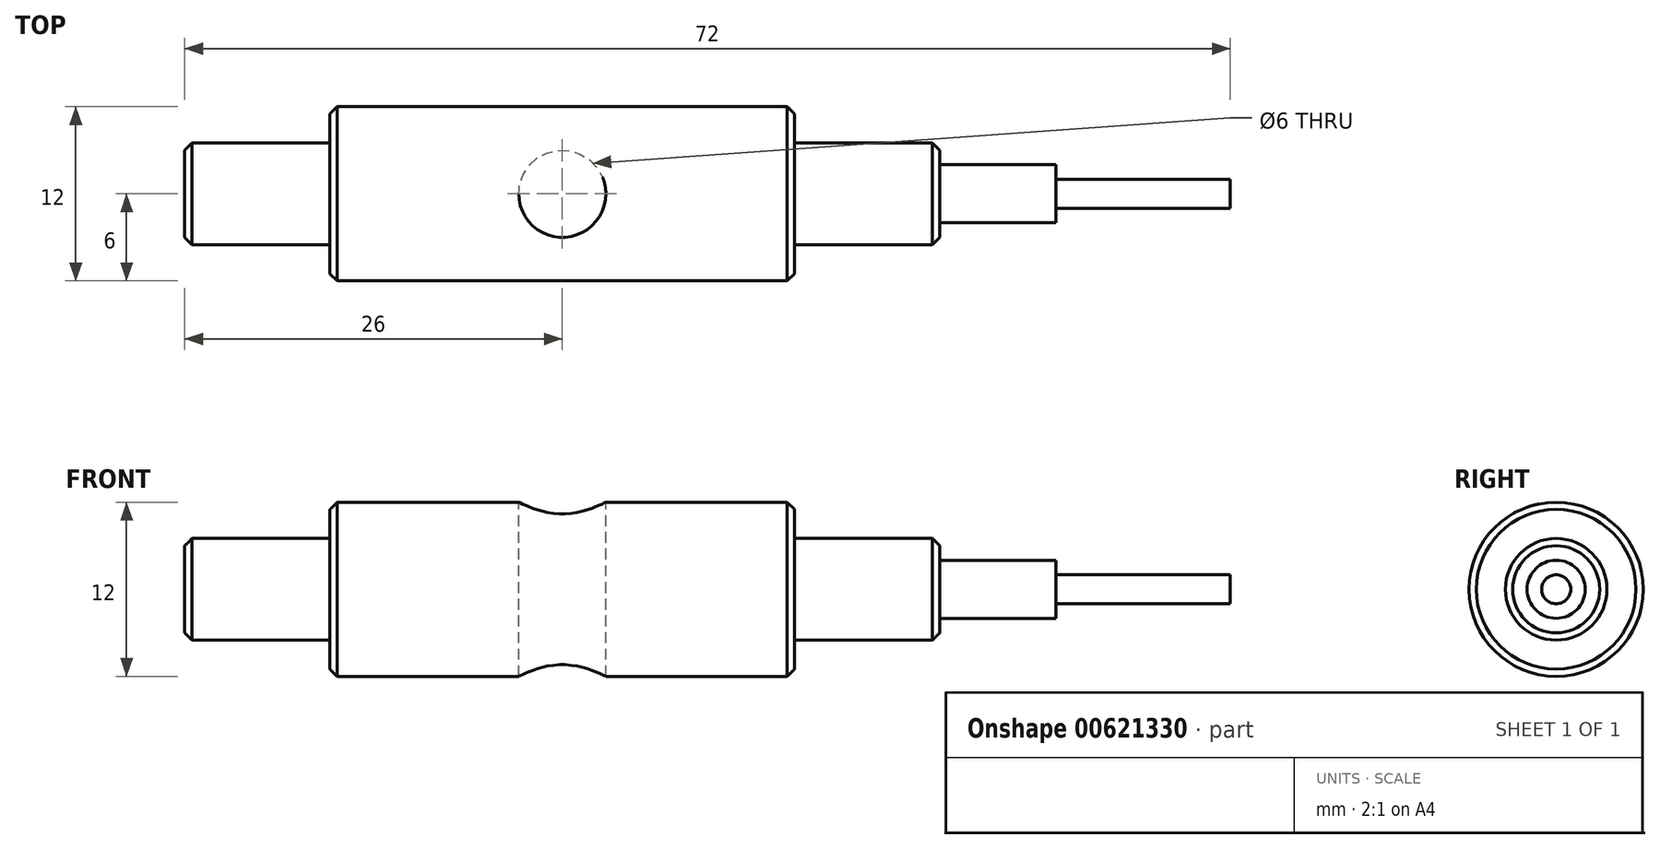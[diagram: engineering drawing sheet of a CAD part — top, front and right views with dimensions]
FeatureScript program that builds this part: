
annotation { "Feature Type Name" : "Feature", "Feature Type Description" : "" }
export const myFeature = defineFeature(function(context is Context, id is Id, definition is map)
    precondition{}
    {
        {
            var Q0;
            Q0=qCreatedBy(makeId("Front.planeOp"),FACE);
            var sketch = newSketch(context, id + "F0", { "sketchPlane" : qUnion([Q0])});
            skLineSegment(sketch, "E0", {"start": v(0, 0) * mm, "end": v(74.72, 0) * mm, "construction": true});
            skLineSegment(sketch, "E1", {"start": v(0, 0) * mm, "end": v(0, 3.5) * mm});
            skLineSegment(sketch, "E2", {"start": v(0, 3.5) * mm, "end": v(10, 3.5) * mm});
            skLineSegment(sketch, "E3", {"start": v(10, 3.5) * mm, "end": v(10, 6) * mm});
            skLineSegment(sketch, "E4", {"start": v(10, 6) * mm, "end": v(42, 6) * mm});
            skLineSegment(sketch, "E5", {"start": v(42, 6) * mm, "end": v(42, 3.5) * mm});
            skLineSegment(sketch, "E6", {"start": v(42, 3.5) * mm, "end": v(52, 3.5) * mm});
            skLineSegment(sketch, "E7", {"start": v(52, 3.5) * mm, "end": v(52, 2) * mm});
            skLineSegment(sketch, "E8", {"start": v(72, 0) * mm, "end": v(0, 0) * mm});
            skLineSegment(sketch, "E9", {"start": v(72, 1) * mm, "end": v(72, 0) * mm});
            skLineSegment(sketch, "E10", {"start": v(72, 1) * mm, "end": v(60, 1) * mm});
            skLineSegment(sketch, "E11", {"start": v(60, 1) * mm, "end": v(60, 2) * mm});
            skLineSegment(sketch, "E12", {"start": v(60, 2) * mm, "end": v(52, 2) * mm});
            skSolve(sketch);
        }
        {
            var Q0;
            Q0 = qSketchRegion(id + "F0", true);
            var Q1;
            Q1=sQuery(id+"F0.wireOp",EDGE,"E0");
            revolve(context, id + "F1", {"entities" : qUnion([Q0]), "axis" : qUnion([Q1]), "revolveType" : RevolveType.FULL});
        }
        {
            var Q0;
            Q0=qCreatedBy(makeId("Top.planeOp"),FACE);
            var sketch = newSketch(context, id + "F2", { "sketchPlane" : qUnion([Q0])});
            skCircle(sketch, "E13", {"center": v(26, 0) * mm, "radius": 3 * mm});
            skSolve(sketch);
        }
        {
            var Q0;
            Q0 = qSketchRegion(id + "F2", true);
            extrude(context, id + "F3", {"entities" : qUnion([Q0]), "operationType" : NewBodyOperationType.REMOVE, "endBound" : BoundingType.THROUGH_ALL, "oppositeDirection" : true, "depth" : 25 * mm, "offsetDistance" : 25 * mm, "hasSecondDirection" : true, "secondDirectionBound" : SecondDirectionBoundingType.THROUGH_ALL, "secondDirectionOppositeDirection" : false, "secondDirectionDepth" : 25 * mm});
        }
        {
            var Q0;
            Q0=makeQuery(id+"F1.opRevolve","SWEPT_EDGE",EDGE,{"disambiguationData":[OSD([sQuery(id+"F0.wireOp",EDGE,"E6"),sQuery(id+"F0.wireOp",EDGE,"E7")])]});
            var Q1;
            Q1=makeQuery(id+"F1.opRevolve","SWEPT_EDGE",EDGE,{"disambiguationData":[OSD([sQuery(id+"F0.wireOp",EDGE,"E1"),sQuery(id+"F0.wireOp",EDGE,"E2")])]});
            var Q2;
            Q2=makeQuery(id+"F1.opRevolve","SWEPT_EDGE",EDGE,{"disambiguationData":[OSD([sQuery(id+"F0.wireOp",EDGE,"E3"),sQuery(id+"F0.wireOp",EDGE,"E4")])]});
            var Q3;
            Q3=makeQuery(id+"F1.opRevolve","SWEPT_EDGE",EDGE,{"disambiguationData":[OSD([sQuery(id+"F0.wireOp",EDGE,"E4"),sQuery(id+"F0.wireOp",EDGE,"E5")])]});
            chamfer(context, id + "F4", {"entities" : qUnion([Q0, Q1, Q2, Q3]), "width" : .5 * mm, "tangentPropagation" : true});
        }
    });
